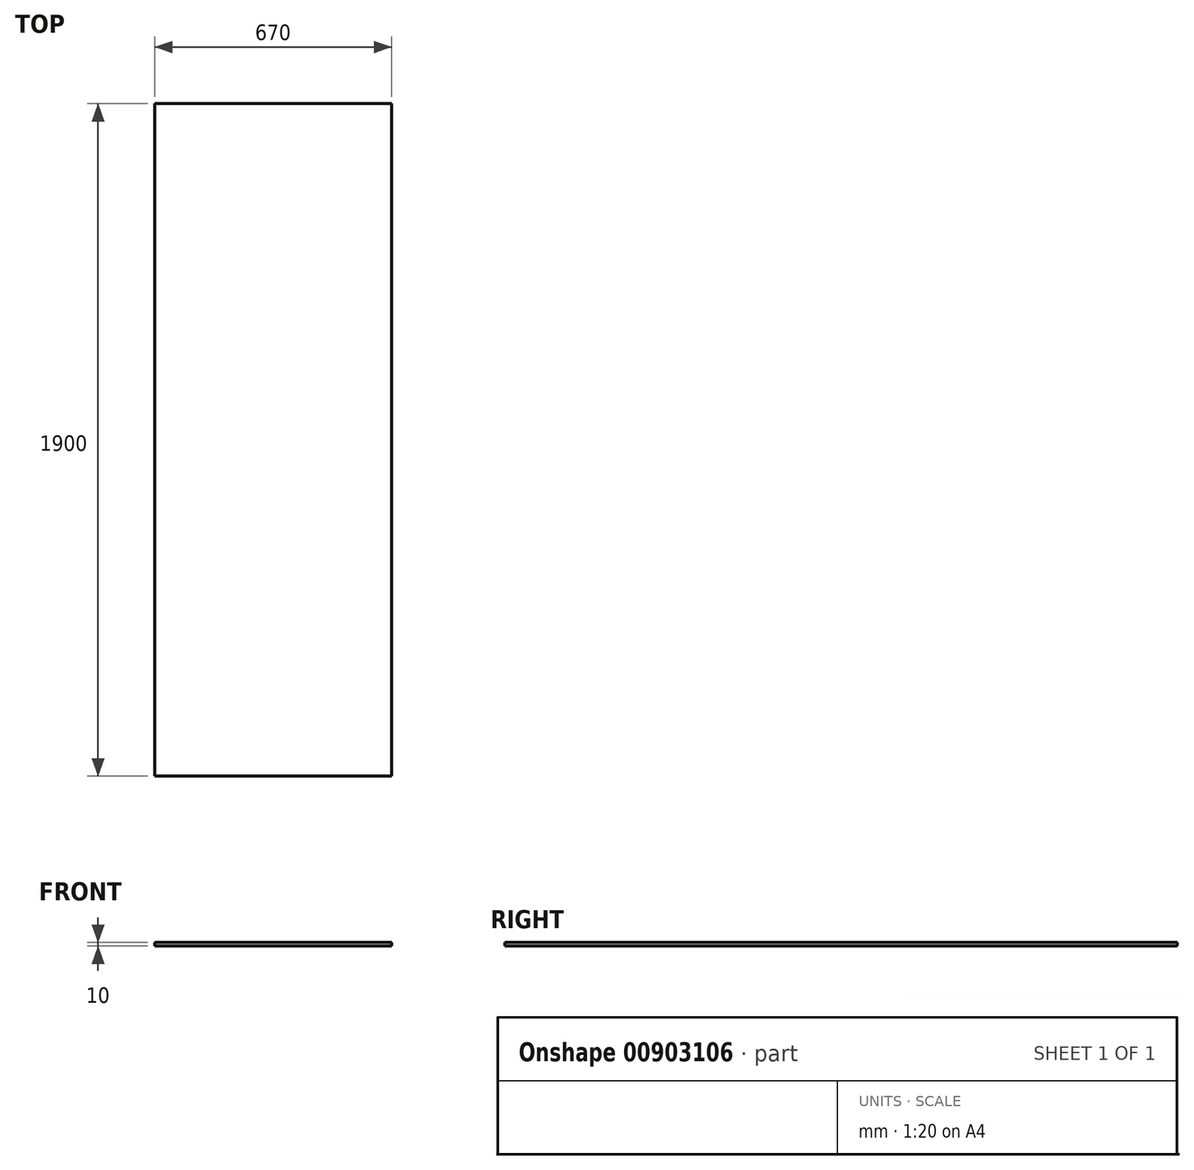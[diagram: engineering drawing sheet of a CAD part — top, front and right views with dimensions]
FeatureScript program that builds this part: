
annotation { "Feature Type Name" : "Feature", "Feature Type Description" : "" }
export const myFeature = defineFeature(function(context is Context, id is Id, definition is map)
    precondition{}
    {
        {
            var Q0;
            Q0=qCreatedBy(makeId("Top.planeOp"),FACE);
            var sketch = newSketch(context, id + "F0", { "sketchPlane" : qUnion([Q0])});
            skLineSegment(sketch, "E0.bottom", {"start": v(-279.47, 1783.4) * mm, "end": v(390.53, 1783.4) * mm});
            skLineSegment(sketch, "E0.top", {"start": v(-279.47, -116.6) * mm, "end": v(390.53, -116.6) * mm});
            skLineSegment(sketch, "E0.left", {"start": v(-279.47, 1783.4) * mm, "end": v(-279.47, -116.6) * mm});
            skLineSegment(sketch, "E0.right", {"start": v(390.53, 1783.4) * mm, "end": v(390.53, -116.6) * mm});
            skSolve(sketch);
        }
        {
            var Q0;
            Q0=makeQuery(id+"F0.imprint","IMPRINT",FACE,{"disambiguationData":[TD([[makeQuery(id+"F0.imprint","IMPRINT",EDGE,{"derivedFrom":sQuery(id+"F0.wireOp",EDGE,"E0.bottom")}),-1.0]])]});
            extrude(context, id + "F1", {"entities" : qUnion([Q0]), "depth" : 10 * mm, "offsetDistance" : 25 * mm});
        }
    });
